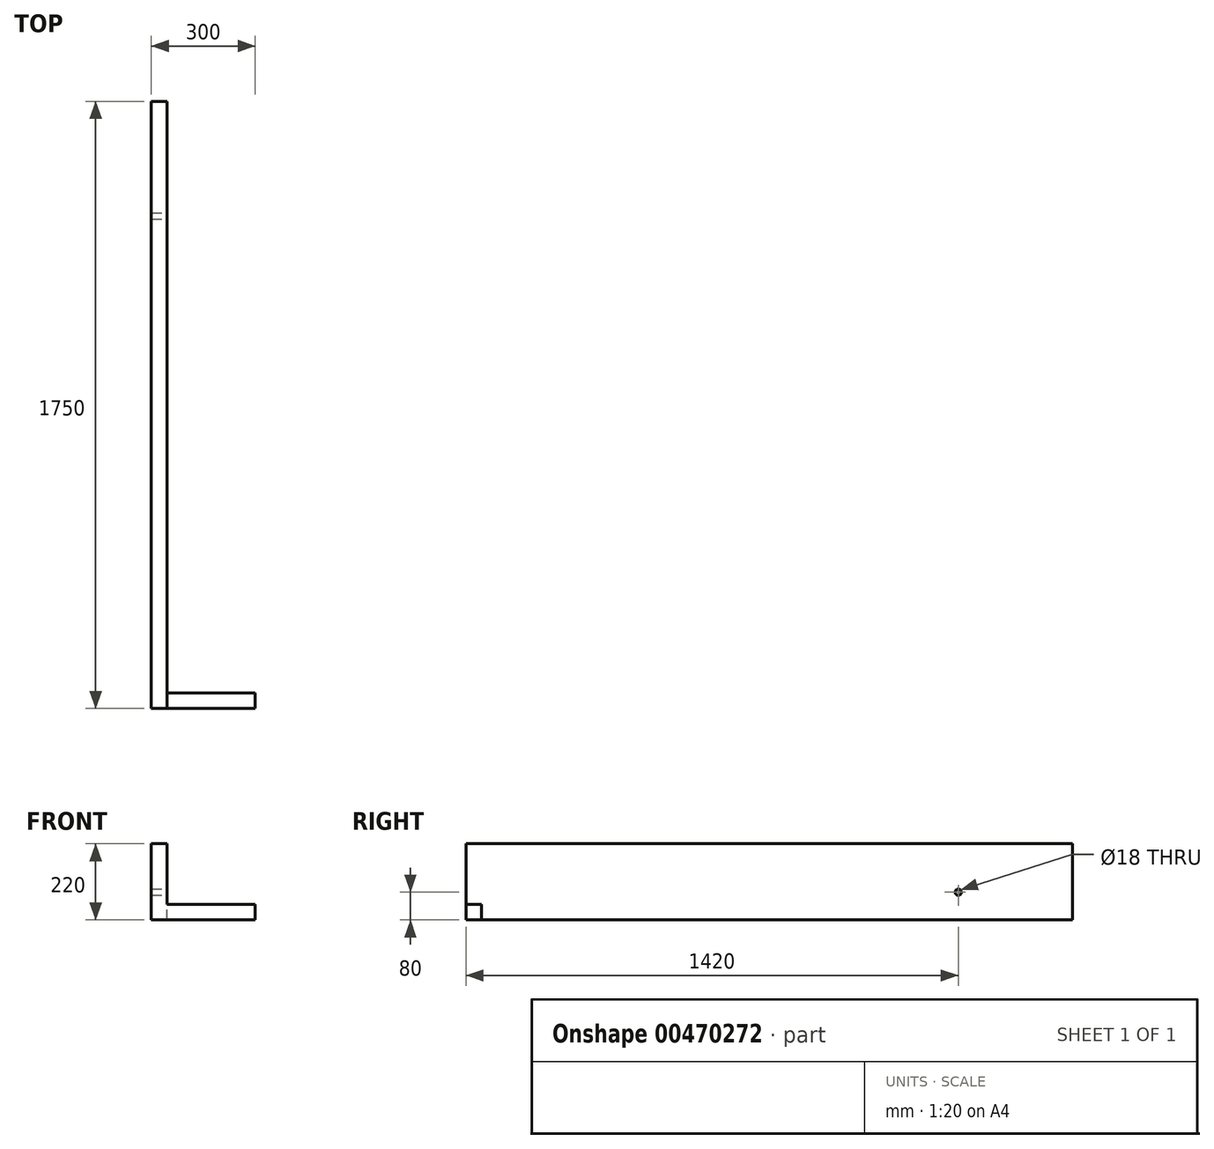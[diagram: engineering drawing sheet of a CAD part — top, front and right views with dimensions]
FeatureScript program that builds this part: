
annotation { "Feature Type Name" : "Feature", "Feature Type Description" : "" }
export const myFeature = defineFeature(function(context is Context, id is Id, definition is map)
    precondition{}
    {
        {
            var Q0;
            Q0=qCreatedBy(makeId("Front.planeOp"),FACE);
            var sketch = newSketch(context, id + "F0", { "sketchPlane" : qUnion([Q0])});
            skLineSegment(sketch, "E0.bottom", {"start": v(-255, 0) * mm, "end": v(-300, 0) * mm});
            skLineSegment(sketch, "E0.top", {"start": v(-255, 220) * mm, "end": v(-300, 220) * mm});
            skLineSegment(sketch, "E0.left", {"start": v(-255, 0) * mm, "end": v(-255, 220) * mm});
            skLineSegment(sketch, "E0.right", {"start": v(-300, 0) * mm, "end": v(-300, 220) * mm});
            skLineSegment(sketch, "E1.bottom", {"start": v(-255, 0) * mm, "end": v(0, 0) * mm});
            skLineSegment(sketch, "E1.top", {"start": v(-255, 45) * mm, "end": v(0, 45) * mm});
            skLineSegment(sketch, "E1.left", {"start": v(-255, 0) * mm, "end": v(-255, 45) * mm});
            skLineSegment(sketch, "E1.right", {"start": v(0, 0) * mm, "end": v(0, 45) * mm});
            skSolve(sketch);
        }
        {
            var Q0;
            Q0=makeQuery(id+"F0.imprint","IMPRINT",FACE,{"disambiguationData":[TD([[makeQuery(id+"F0.imprint","IMPRINT",EDGE,{"derivedFrom":sQuery(id+"F0.wireOp",EDGE,"E0.bottom")}),-1.0]])]});
            extrude(context, id + "F1", {"entities" : qUnion([Q0]), "oppositeDirection" : true, "depth" : 1750 * mm});
        }
        {
            var Q0;
            Q0=makeQuery(id+"F0.imprint","IMPRINT",FACE,{"disambiguationData":[TD([[makeQuery(id+"F0.imprint","IMPRINT",EDGE,{"derivedFrom":sQuery(id+"F0.wireOp",EDGE,"E1.bottom")}),1.0]])]});
            extrude(context, id + "F2", {"entities" : qUnion([Q0]), "operationType" : NewBodyOperationType.ADD, "oppositeDirection" : true, "depth" : 45 * mm});
        }
        {
            var Q0;
            Q0=qCreatedBy(makeId("Right.planeOp"),FACE);
            var sketch = newSketch(context, id + "F3", { "sketchPlane" : qUnion([Q0])});
            skCircle(sketch, "E2", {"center": v(1420, 80) * mm, "radius": 9 * mm});
            skSolve(sketch);
        }
        {
            var Q0;
            Q0 = qSketchRegion(id + "F3", true);
            extrude(context, id + "F4", {"entities" : qUnion([Q0]), "operationType" : NewBodyOperationType.REMOVE, "endBound" : BoundingType.THROUGH_ALL, "oppositeDirection" : true, "depth" : 25 * mm});
        }
    });
